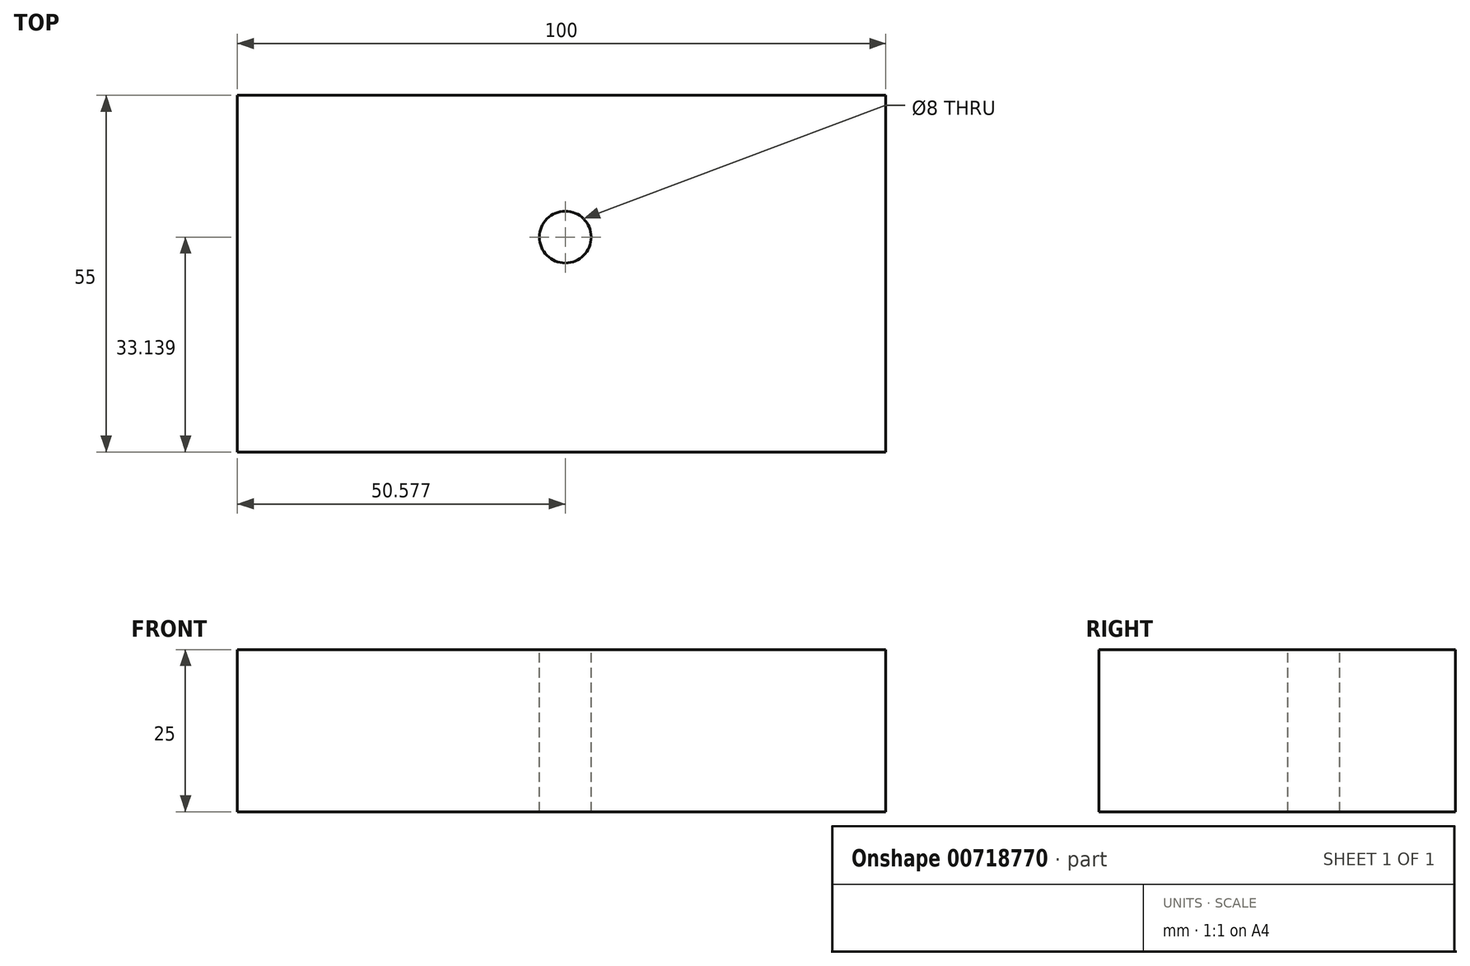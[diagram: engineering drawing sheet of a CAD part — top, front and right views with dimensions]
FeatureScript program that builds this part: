
annotation { "Feature Type Name" : "Feature", "Feature Type Description" : "" }
export const myFeature = defineFeature(function(context is Context, id is Id, definition is map)
    precondition{}
    {
        {
            var Q0;
            Q0=qCreatedBy(makeId("Top.planeOp"),FACE);
            var sketch = newSketch(context, id + "F0", { "sketchPlane" : qUnion([Q0])});
            skLineSegment(sketch, "E0.bottom", {"start": v(-100, 55) * mm, "end": v(0, 55) * mm});
            skLineSegment(sketch, "E0.top", {"start": v(-100, 0) * mm, "end": v(0, 0) * mm});
            skLineSegment(sketch, "E0.left", {"start": v(-100, 55) * mm, "end": v(-100, 0) * mm});
            skLineSegment(sketch, "E0.right", {"start": v(0, 55) * mm, "end": v(0, 0) * mm});
            skSolve(sketch);
        }
        {
            var Q0;
            Q0 = qSketchRegion(id + "F0", true);
            extrude(context, id + "F1", {"entities" : qUnion([Q0]), "depth" : 25 * mm, "offsetDistance" : 25 * mm});
        }
        {
            var Q0;
            Q0=makeQuery(id+"F1.opExtrude","CAP_FACE",FACE,{"disambiguationData":[OSD([sQuery(id+"F0.wireOp",EDGE,"E0.bottom"),sQuery(id+"F0.wireOp",EDGE,"E0.top"),sQuery(id+"F0.wireOp",EDGE,"E0.left"),sQuery(id+"F0.wireOp",EDGE,"E0.right")])],"isStart":false});
            var sketch = newSketch(context, id + "F2", { "sketchPlane" : qUnion([Q0])});
            skCircle(sketch, "E1", {"center": v(-79.42, 33.14) * mm, "radius": 4 * mm});
            skCircle(sketch, "E2.1.0.0", {"center": v(-49.42, 33.14) * mm, "radius": 4 * mm});
            skCircle(sketch, "E2.2.0.0", {"center": v(-19.42, 33.14) * mm, "radius": 4 * mm});
            skLineSegment(sketch, "E2.direction1", {"start": v(-79.42, 33.14) * mm, "end": v(-49.42, 33.14) * mm, "construction": true});
            skSolve(sketch);
        }
        {
            var Q0;
            Q0=makeQuery(id+"F2.imprint","IMPRINT",FACE,{"disambiguationData":[TD([[makeQuery(id+"F2.imprint","IMPRINT",EDGE,{"derivedFrom":sQuery(id+"F2.wireOp",EDGE,"E2.1.0.0")}),1.0]])]});
            extrude(context, id + "F3", {"entities" : qUnion([Q0]), "operationType" : NewBodyOperationType.REMOVE, "oppositeDirection" : true, "depth" : 25 * mm, "offsetDistance" : 25 * mm});
        }
    });
